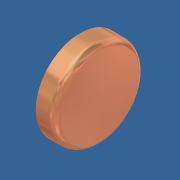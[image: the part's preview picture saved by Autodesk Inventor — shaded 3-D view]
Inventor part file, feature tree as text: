
AUTODESK INVENTOR PART (.ipt)
format: ipt  version: unknown  size: 224,768 bytes
history: native  units: mm
features: revolve x1, shell x1, sketch x1
ambient origin geometry x8: Origin, YZ Plane, XZ Plane, XY Plane, X Axis, Y Axis, Z Axis, Center Point
feature tree (3):
  revolve  "Вращение1"
  shell  "Оболочка1"  Thickness=90.0deg
  sketch  "Эскиз1"
